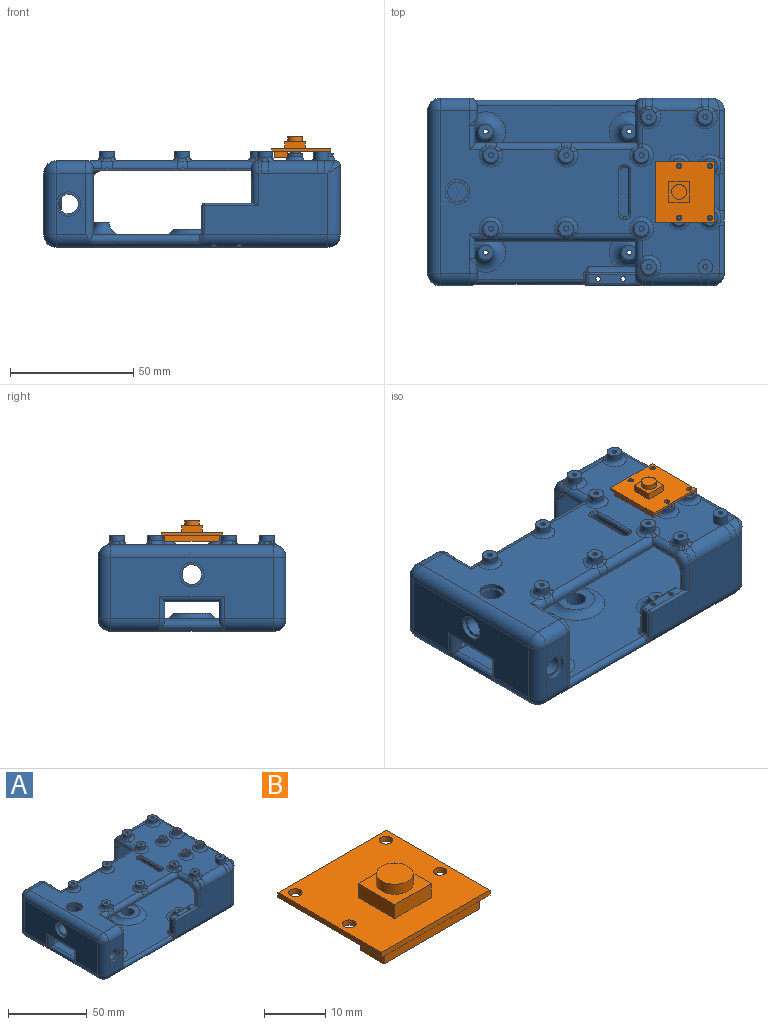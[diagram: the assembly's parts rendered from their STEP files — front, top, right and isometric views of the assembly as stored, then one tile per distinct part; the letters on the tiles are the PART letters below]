
ASSEMBLY  parts=2 mates=1
PART A: 360 faces, bbox 123.4x78.5x40.3 mm
  f0: plane 28x10mm, normal (1,0,0), area 97.8mm2, adj f1,f355,f356,f357,f358,f359
  f1: torus R=7mm, axis (-1,0,0), area 28.3mm2, adj f0,f2,f355,f359
  f2: cylinder r=5mm len=5mm, axis (-1,0,0), area 15.7mm2, adj f1,f3,f353,f354
  f3: plane 16x2mm, normal (0,-1,0), area 32mm2, adj f2,f4,f352,f359
  f4: cylinder r=2mm len=16mm, axis (0,0,1), area 50.3mm2, adj f3,f5,f351,f354
  f5: plane 26x7.1mm, normal (-1,0,0), area 125.8mm2, adj f4,f6,f348,f349,f350,f351,f353,f354
  f6: plane 112.82x71.05mm, normal (0,0,1), area 5628.9mm2, adj f5,f7,f314,f315,f316,f318,f319,f320
  f7: torus R=7mm, axis (-1,0,0), area 20.9mm2, adj f6,f8,f314,f344
  f8: cylinder r=2mm len=16mm, axis (0,0,1), area 50.3mm2, adj f7,f9,f313,f314
  f9: plane 16x2mm, normal (0,1,0), area 32mm2, adj f8,f10,f312,f344
  f10: cylinder r=2mm len=16mm, axis (0,0,-1), area 50.3mm2, adj f9,f11,f309,f310
  f11: plane 28x10mm, normal (1,0,0), area 97.8mm2, adj f10,f12,f309,f310,f355,f357
  f12: cylinder r=5mm len=28mm, axis (0,0,-1), area 208.1mm2, adj f11,f13,f307,f308
  f13: sphere r=5mm, area 39.3mm2, adj f12,f14,f357
  f14: cylinder r=5mm len=110mm, axis (1,0,0), area 689.2mm2, adj f13,f15,f288,f289,f304,f305,f306,f307
  f15: cylinder r=1mm len=17.66mm, axis (0,0,1), area 108.2mm2, adj f14,f16
  f16: plane 20.27x3.4mm, normal (0,0,1), area 59.2mm2, adj f15,f17,f274,f275,f276,f285,f286,f287
  f17: plane 30x16mm, normal (0,1,0), area 469.6mm2, adj f16,f18,f274,f287,f314,f316
  f18: cylinder r=5mm len=29mm, axis (1,0,0), area 227.4mm2, adj f17,f19,f20,f314,f353
  f19: bspline ~4.02x2.53mm, area 6.1mm2, adj f18,f20,f274,f275
  f20: torus R=6mm, axis (1,0,0), area 8.3mm2, adj f18,f19,f21,f273
  f21: cylinder r=1mm len=10mm, axis (0,-1,0), area 15.7mm2, adj f20,f22,f272,f273,f353
  f22: cylinder r=3mm len=9.84mm, axis (0,1,0), area 42.6mm2, adj f21,f23,f46,f47,f214,f215
  f23: bspline ~4.03x2.8mm, area 5.5mm2, adj f22,f24,f41,f45
  f24: bspline ~3.52x1.71mm, area 5.2mm2, adj f23,f25,f41,f46
  f25: bspline ~2.95x2.06mm, area 1.9mm2, adj f24,f26,f40,f41
  f26: cylinder r=3mm len=2.85mm, axis (0,1,0), area 3.6mm2, adj f25,f27,f46,f273
  f27: torus R=2mm, axis (1,0,0), area 28.4mm2, adj f26,f28,f40,f273,f275
  f28: cylinder r=5mm len=4.88mm, axis (1,0,0), area 7mm2, adj f27,f29,f39,f307
  f29: bspline ~3.05x2.15mm, area 2.1mm2, adj f28,f30,f40,f41
  f30: bspline ~3.36x1.78mm, area 5.2mm2, adj f29,f31,f39,f41
  f31: bspline ~4.17x3.08mm, area 6mm2, adj f30,f32,f41,f45
  f32: cylinder r=5mm len=19.94mm, axis (1,0,0), area 154.7mm2, adj f31,f33,f39,f215,f307
  f33: bspline ~5.28x5.26mm, area 22.2mm2, adj f32,f34,f38,f307
  f34: cylinder r=3mm len=6mm, axis (0,0,-1), area 75.4mm2, adj f33,f35,f215
  f35: plane 6x6mm, normal (0,0,1), area 25.1mm2, adj f34,f36
  f36: cylinder r=1mm len=4mm, axis (0,0,-1), area 25.1mm2, adj f35,f37
  f37: plane 2x2mm, normal (0,0,1), area 3.1mm2, adj f36
  f38: cylinder r=5mm len=5mm, axis (1,0,0), area 24.1mm2, adj f33,f215,f307,f308
  f39: bspline ~5.28x5.26mm, area 18.1mm2, adj f28,f30,f32,f307
  f40: bspline ~2.93x2.68mm, area 3.1mm2, adj f25,f27,f29,f41
  f41: cylinder r=3mm len=6mm, axis (0,0,-1), area 44.3mm2, adj f23,f24,f25,f29,f30,f31,f40,f42
  f42: plane 6x6mm, normal (0,0,1), area 25.1mm2, adj f41,f43
  f43: cylinder r=1mm len=4mm, axis (0,0,-1), area 25.1mm2, adj f42,f44
  f44: plane 2x2mm, normal (0,0,1), area 3.1mm2, adj f43
  f45: torus R=4.8mm, axis (0,0,1), area 27.9mm2, adj f23,f31,f41,f215
  f46: bspline ~4.49x3.34mm, area 10.4mm2, adj f22,f24,f26,f273
  f47: cylinder r=3mm len=27.11mm, axis (1,0,0), area 120.5mm2, adj f22,f48,f207,f208,f214,f215,f272
  f48: bspline ~4.91x3.2mm, area 12.2mm2, adj f47,f49,f206,f272
  f49: cylinder r=3mm len=26.23mm, axis (1,0,0), area 120.5mm2, adj f48,f50,f199,f200,f215,f272
  f50: bspline ~4.91x3.2mm, area 12.2mm2, adj f49,f51,f198,f272
  f51: cylinder r=3mm len=6.46mm, axis (1,0,0), area 24.8mm2, adj f50,f52,f192,f215,f272
  f52: cylinder r=2mm len=10mm, axis (0,-1,0), area 50.3mm2, adj f51,f53,f215,f272,f353
  f53: bspline ~4.71x4.31mm, area 19.5mm2, adj f52,f54,f190,f191
  f54: cylinder r=3mm len=6mm, axis (0,-1,0), area 19.8mm2, adj f53,f55,f215,f323
  f55: torus R=2mm, axis (-1,0,0), area 28.9mm2, adj f54,f56,f322,f323
  f56: cylinder r=5mm len=12mm, axis (1,0,0), area 94.2mm2, adj f55,f57,f215,f305
  f57: sphere r=5mm, area 39.3mm2, adj f56,f58,f189
  f58: cylinder r=5mm len=25mm, axis (0,0,1), area 196.3mm2, adj f57,f59,f304,f305
  f59: plane 66x25mm, normal (-1,0,0), area 1337.5mm2, adj f58,f60,f180,f181,f186,f187,f188,f189
  f60: cylinder r=5mm len=10mm, axis (1,0,0), area 56.5mm2, adj f59,f61
  f61: plane 10x10mm, normal (-1,0,0), area 28.3mm2, adj f60,f62
  f62: cylinder r=4mm len=8mm, axis (1,0,0), area 138.2mm2, adj f61,f63
  f63: plane 16.26x13.46mm, normal (1,0,0), area 103.7mm2, adj f62,f64,f171,f172,f177,f178,f179
  f64: plane 15x12.2mm, normal (0,0,-1), area 103.7mm2, adj f63,f65,f68
  f65: cylinder r=4mm len=8mm, axis (0,0,-1), area 138.2mm2, adj f64,f66
  f66: plane 10x10mm, normal (0,0,1), area 28.3mm2, adj f65,f67
  f67: cylinder r=5mm len=10mm, axis (0,0,-1), area 56.5mm2, adj f66,f215
  f68: torus R=12.2mm, axis (0,0,1), area 222.9mm2, adj f64,f69,f70,f159,f170,f171,f179,f353
  f69: sphere r=5mm, area 20.7mm2, adj f68,f70,f171,f172
  f70: cylinder r=5mm len=21.5mm, axis (0,-1,0), area 153.7mm2, adj f68,f69,f71,f158,f332,f353
  f71: torus R=10.86mm, axis (0,1,0), area 104.7mm2, adj f70,f72,f154,f155,f158,f332,f333
  f72: bspline ~15.69x2.44mm, area 38.6mm2, adj f71,f73,f334,f335
  f73: cylinder r=2mm len=2mm, axis (0,0,-1), area 3.6mm2, adj f72,f74,f154,f335
  f74: torus R=7mm, axis (-1,0,0), area 18.5mm2, adj f73,f75,f158,f335
  f75: bspline ~4.71x4.31mm, area 19.5mm2, adj f74,f76,f153,f158
  f76: cylinder r=2mm len=10mm, axis (0,-1,0), area 50.3mm2, adj f75,f77,f152,f215,f353
  f77: cylinder r=3mm len=6.46mm, axis (-1,0,0), area 24.8mm2, adj f76,f78,f151,f152,f215
  f78: bspline ~4.91x3.2mm, area 12.2mm2, adj f77,f79,f150,f152
  f79: cylinder r=3mm len=26.23mm, axis (-1,0,0), area 120.5mm2, adj f78,f80,f143,f144,f152,f215
  f80: bspline ~4.91x3.2mm, area 12.2mm2, adj f79,f81,f142,f152
  f81: cylinder r=3mm len=27.11mm, axis (-1,0,0), area 120.5mm2, adj f80,f82,f88,f135,f141,f152,f215
  f82: bspline ~3.84x2.84mm, area 5.2mm2, adj f81,f83,f84,f142
  f83: torus R=4.8mm, axis (0,0,1), area 41.9mm2, adj f82,f84,f143,f215
  f84: cylinder r=3mm len=6mm, axis (0,0,-1), area 43.9mm2, adj f82,f83,f85,f142,f143
  f85: plane 6x6mm, normal (0,0,1), area 25.1mm2, adj f84,f86
  f86: cylinder r=1mm len=4mm, axis (0,0,-1), area 25.1mm2, adj f85,f87
  f87: plane 2x2mm, normal (0,0,1), area 3.1mm2, adj f86
  f88: cylinder r=3mm len=9.84mm, axis (0,1,0), area 42.6mm2, adj f81,f89,f133,f134,f135,f215
  f89: cylinder r=1mm len=10mm, axis (0,-1,0), area 15.7mm2, adj f88,f90,f129,f152,f353
  f90: plane 6.25x2.72mm, normal (-1,0,0), area 3.2mm2, adj f89,f91,f128,f129,f133,f338
  f91: torus R=2mm, axis (1,0,0), area 28.4mm2, adj f90,f92,f127,f128,f338
  f92: cylinder r=5mm len=4.88mm, axis (1,0,0), area 7mm2, adj f91,f93,f125,f126
  f93: plane 28x25.01mm, normal (0,1,0), area 700mm2, adj f92,f94,f104,f105,f115,f125,f338,f356
  f94: cylinder r=5mm len=5mm, axis (1,0,0), area 22.2mm2, adj f93,f95,f103,f104,f215
  f95: bspline ~4.17x3.08mm, area 6mm2, adj f94,f96,f98,f99
  f96: torus R=4.8mm, axis (0,0,1), area 44.4mm2, adj f95,f97,f99,f215
  f97: bspline ~4.17x3.08mm, area 6mm2, adj f96,f98,f99,f105
  f98: bspline ~3.36x1.78mm, area 5.2mm2, adj f95,f97,f99,f104
  f99: cylinder r=3mm len=6mm, axis (0,0,-1), area 42.6mm2, adj f95,f96,f97,f98,f100
  f100: plane 6x6mm, normal (0,0,1), area 25.1mm2, adj f99,f101
  f101: cylinder r=1mm len=4mm, axis (0,0,-1), area 25.1mm2, adj f100,f102
  f102: plane 2x2mm, normal (0,0,1), area 3.1mm2, adj f101
  f103: bspline ~5.23x5mm, area 10.8mm2, adj f94,f355,f356
  f104: bspline ~5.28x5.26mm, area 18.1mm2, adj f93,f94,f98,f105
  f105: cylinder r=5mm len=19.94mm, axis (1,0,0), area 152.9mm2, adj f93,f97,f104,f106,f125,f215
  f106: bspline ~4.17x3.08mm, area 6mm2, adj f105,f107,f108,f109
  f107: torus R=4.8mm, axis (0,0,1), area 27.9mm2, adj f106,f109,f134,f215
  f108: bspline ~3.36x1.78mm, area 5.2mm2, adj f106,f109,f125,f126
  f109: cylinder r=3mm len=6mm, axis (0,0,-1), area 44.3mm2, adj f106,f107,f108,f110,f111,f114,f126,f127
  f110: bspline ~3.26x1.69mm, area 5.2mm2, adj f109,f114,f133,f134
  f111: plane 6x6mm, normal (0,0,1), area 25.1mm2, adj f109,f112
  f112: cylinder r=1mm len=4mm, axis (0,0,-1), area 25.1mm2, adj f111,f113
  f113: plane 2x2mm, normal (0,0,1), area 3.1mm2, adj f112
  f114: bspline ~2.95x2.06mm, area 1.9mm2, adj f109,f110,f127,f128
  f115: cylinder r=5mm len=110mm, axis (1,0,0), area 617.5mm2, adj f93,f116,f123,f124,f289,f336,f337,f338
  f116: plane 25x12mm, normal (0,1,0), area 221.5mm2, adj f115,f117,f120,f180,f336
  f117: cylinder r=5mm len=10mm, axis (0,-1,0), area 56.5mm2, adj f116,f118
  f118: plane 10x10mm, normal (0,1,0), area 28.3mm2, adj f117,f119
  f119: cylinder r=4mm len=8mm, axis (0,-1,0), area 138.2mm2, adj f118,f155
  f120: cylinder r=5mm len=12mm, axis (1,0,0), area 94.2mm2, adj f116,f121,f122,f215
  f121: sphere r=5mm, area 53.5mm2, adj f120,f180,f189
  f122: torus R=2mm, axis (-1,0,0), area 28.9mm2, adj f120,f153,f335,f336
  f123: sphere r=5mm, area 53.5mm2, adj f115,f180,f188
  f124: sphere r=5mm, area 25mm2, adj f115,f356,f357
  f125: bspline ~5.28x5.26mm, area 18.1mm2, adj f92,f93,f105,f108
  f126: bspline ~3.05x2.15mm, area 2.1mm2, adj f92,f108,f109,f127
  f127: bspline ~2.93x2.68mm, area 3.1mm2, adj f91,f109,f114,f126
  f128: cylinder r=3mm len=2.85mm, axis (0,1,0), area 3.6mm2, adj f90,f91,f114,f133
  f129: torus R=6mm, axis (1,0,0), area 8.3mm2, adj f89,f90,f130,f350
  f130: bspline ~4.02x2.53mm, area 6.1mm2, adj f129,f131,f338,f350
  f131: cylinder r=1mm len=16mm, axis (0,0,1), area 33.5mm2, adj f130,f132,f338,f349
  f132: bspline ~4.02x2.53mm, area 6.1mm2, adj f131,f338,f340,f348
  f133: bspline ~4.49x3.34mm, area 10.4mm2, adj f88,f90,f110,f128
  f134: bspline ~4.03x2.8mm, area 5.5mm2, adj f88,f107,f109,f110
  f135: bspline ~2.91x2.77mm, area 4.5mm2, adj f81,f88,f136,f140,f141
  f136: cylinder r=3mm len=6mm, axis (0,0,-1), area 42.5mm2, adj f135,f137,f140,f141
  f137: plane 6x6mm, normal (0,0,1), area 25.1mm2, adj f136,f138
  f138: cylinder r=1mm len=4mm, axis (0,0,-1), area 25.1mm2, adj f137,f139
  f139: plane 2x2mm, normal (0,0,1), area 3.1mm2, adj f138
  f140: torus R=4.8mm, axis (0,0,1), area 52.4mm2, adj f135,f136,f141,f215
  f141: bspline ~4.14x2.91mm, area 6.2mm2, adj f81,f135,f136,f140
  f142: bspline ~4.25x1.65mm, area 6.3mm2, adj f80,f82,f84,f143
  f143: bspline ~3.84x2.84mm, area 5.2mm2, adj f79,f83,f84,f142
  f144: bspline ~3.84x2.84mm, area 5.2mm2, adj f79,f145,f146,f150
  f145: torus R=4.8mm, axis (0,0,1), area 41.9mm2, adj f144,f146,f151,f215
  f146: cylinder r=3mm len=6mm, axis (0,0,-1), area 43.9mm2, adj f144,f145,f147,f150,f151
  f147: plane 6x6mm, normal (0,0,1), area 25.1mm2, adj f146,f148
  f148: cylinder r=1mm len=4mm, axis (0,0,-1), area 25.1mm2, adj f147,f149
  f149: plane 2x2mm, normal (0,0,1), area 3.1mm2, adj f148
  f150: bspline ~4.25x1.65mm, area 6.3mm2, adj f78,f144,f146,f151
  f151: bspline ~3.84x2.84mm, area 5.2mm2, adj f77,f145,f146,f150
  f152: plane 68x1.13mm, normal (0,1,0), area 66.6mm2, adj f76,f77,f78,f79,f80,f81,f89,f353
  f153: cylinder r=3mm len=6mm, axis (0,-1,0), area 19.8mm2, adj f75,f122,f215,f335
  f154: plane 1.24x1.15mm, normal (0,-1,0), area 0.7mm2, adj f71,f73,f158
  f155: plane 15x15mm, normal (0,-1,0), area 126.4mm2, adj f71,f119,f156
  f156: cylinder r=7.5mm len=17.7mm, axis (0,1,0), area 267.7mm2, adj f155,f157,f332
  f157: plane 12.69x3.5mm, normal (0,1,0), area 31.3mm2, adj f156,f332
  f158: cylinder r=5mm len=11.94mm, axis (-1,0,0), area 69.1mm2, adj f70,f71,f74,f75,f154,f353
  f159: cylinder r=5mm len=21.5mm, axis (0,-1,0), area 153.7mm2, adj f68,f160,f170,f190,f326,f353
  f160: torus R=10.86mm, axis (0,-1,0), area 104.7mm2, adj f159,f161,f163,f164,f190,f325,f326
  f161: plane 1.24x1.15mm, normal (0,1,0), area 0.7mm2, adj f160,f162,f190
  f162: cylinder r=2mm len=2mm, axis (0,0,1), area 3.6mm2, adj f161,f163,f191,f323
  f163: bspline ~15.46x2.44mm, area 38.6mm2, adj f160,f162,f323,f324
  f164: plane 15x15mm, normal (0,1,0), area 126.4mm2, adj f160,f165,f167
  f165: cylinder r=7.5mm len=17.7mm, axis (0,-1,0), area 267.7mm2, adj f164,f166,f326
  f166: plane 12.69x3.5mm, normal (0,-1,0), area 31.3mm2, adj f165,f326
  f167: cylinder r=4mm len=8mm, axis (0,1,0), area 138.2mm2, adj f164,f168
  f168: plane 10x10mm, normal (0,-1,0), area 28.3mm2, adj f167,f169
  f169: cylinder r=5mm len=10mm, axis (0,1,0), area 56.5mm2, adj f168,f305
  f170: sphere r=5mm, area 20.7mm2, adj f68,f159,f178,f179
  f171: bspline ~5.35x3.56mm, area 2.6mm2, adj f63,f68,f69
  f172: torus R=10.86mm, axis (-1,0,0), area 40.4mm2, adj f63,f69,f173,f332
  f173: cylinder r=7.5mm len=11.69mm, axis (0,0,1), area 43.2mm2, adj f172,f174,f175,f176,f177,f178,f326,f332
  f174: plane 22x3mm, normal (0,0,-1), area 64.2mm2, adj f173,f175,f176,f186,f328,f330
  f175: cylinder r=1mm len=9.31mm, axis (0,1,0), area 12.4mm2, adj f173,f174,f331,f332
  f176: cylinder r=1mm len=9.31mm, axis (0,1,0), area 12.4mm2, adj f173,f174,f326,f327
  f177: cylinder r=7.5mm len=11.69mm, axis (1,0,0), area 0mm2, adj f63,f173
  f178: torus R=10.86mm, axis (-1,0,0), area 40.4mm2, adj f63,f170,f173,f326
  f179: bspline ~5.35x3.56mm, area 2.6mm2, adj f63,f68,f170
  f180: cylinder r=5mm len=25mm, axis (0,0,1), area 196.3mm2, adj f59,f116,f121,f123
  f181: cylinder r=2mm len=9mm, axis (0,0,-1), area 25.1mm2, adj f59,f182,f186,f328
  f182: torus R=3mm, axis (0,-1,0), area 9mm2, adj f181,f183,f188,f328
  f183: cylinder r=2mm len=26mm, axis (0,-1,0), area 120.1mm2, adj f182,f184,f185,f188,f328,f330
  f184: torus R=3mm, axis (0,-1,0), area 9mm2, adj f183,f187,f188,f330
  f185: plane 22x21.66mm, normal (0,0,1), area 476.5mm2, adj f183,f328,f329,f330
  f186: cylinder r=2mm len=26mm, axis (0,-1,0), area 75.4mm2, adj f59,f174,f181,f187
  f187: cylinder r=2mm len=9mm, axis (0,0,1), area 25.1mm2, adj f59,f184,f186,f330
  f188: cylinder r=5mm len=66mm, axis (0,-1,0), area 390.3mm2, adj f59,f123,f182,f183,f184,f289,f304
  f189: cylinder r=5mm len=66mm, axis (0,-1,0), area 518.4mm2, adj f57,f59,f121,f215
  f190: cylinder r=5mm len=11.94mm, axis (1,0,0), area 69.1mm2, adj f53,f159,f160,f161,f191,f353
  f191: torus R=7mm, axis (-1,0,0), area 18.5mm2, adj f53,f162,f190,f323
  f192: bspline ~3.84x2.84mm, area 5.2mm2, adj f51,f193,f194,f198
  f193: torus R=4.8mm, axis (0,0,1), area 41.9mm2, adj f192,f194,f199,f215
  f194: cylinder r=3mm len=6mm, axis (0,0,-1), area 43.9mm2, adj f192,f193,f195,f198,f199
  f195: plane 6x6mm, normal (0,0,1), area 25.1mm2, adj f194,f196
  f196: cylinder r=1mm len=4mm, axis (0,0,-1), area 25.1mm2, adj f195,f197
  f197: plane 2x2mm, normal (0,0,1), area 3.1mm2, adj f196
  f198: bspline ~4.4x1.66mm, area 6.3mm2, adj f50,f192,f194,f199
  f199: bspline ~3.84x2.84mm, area 5.2mm2, adj f49,f193,f194,f198
  f200: bspline ~3.84x2.84mm, area 5.2mm2, adj f49,f201,f202,f206
  f201: torus R=4.8mm, axis (0,0,1), area 41.9mm2, adj f200,f202,f207,f215
  f202: cylinder r=3mm len=6mm, axis (0,0,-1), area 43.9mm2, adj f200,f201,f203,f206,f207
  f203: plane 6x6mm, normal (0,0,1), area 25.1mm2, adj f202,f204
  f204: cylinder r=1mm len=4mm, axis (0,0,-1), area 25.1mm2, adj f203,f205
  f205: plane 2x2mm, normal (0,0,1), area 3.1mm2, adj f204
  f206: bspline ~4.4x1.66mm, area 6.3mm2, adj f48,f200,f202,f207
  f207: bspline ~3.84x2.84mm, area 5.2mm2, adj f47,f201,f202,f206
  f208: bspline ~4.14x2.91mm, area 6.2mm2, adj f47,f209,f210,f214
  f209: torus R=4.8mm, axis (0,0,1), area 52.4mm2, adj f208,f210,f214,f215
  f210: cylinder r=3mm len=6mm, axis (0,0,-1), area 42.5mm2, adj f208,f209,f211,f214
  f211: plane 6x6mm, normal (0,0,1), area 25.1mm2, adj f210,f212
  f212: cylinder r=1mm len=4mm, axis (0,0,-1), area 25.1mm2, adj f211,f213
  f213: plane 2x2mm, normal (0,0,1), area 3.1mm2, adj f212
  f214: bspline ~2.91x2.77mm, area 4.5mm2, adj f22,f47,f208,f209,f210
  f215: plane 113x66mm, normal (0,0,1), area 4218.9mm2, adj f22,f32,f34,f38,f45,f47,f49,f51
  f216: torus R=4.8mm, axis (0,0,1), area 63.3mm2, adj f215,f217,f223
  f217: cylinder r=3mm len=6mm, axis (0,0,-1), area 22.6mm2, adj f216,f218
  f218: plane 6x6mm, normal (0,0,1), area 15.7mm2, adj f217,f219
  f219: cylinder r=2mm len=4mm, axis (0,0,1), area 12.6mm2, adj f218,f220
  f220: plane 4x4mm, normal (0,0,1), area 11.4mm2, adj f219,f221
  f221: cylinder r=0.6mm len=4mm, axis (0,0,1), area 15.1mm2, adj f220,f222
  f222: plane 1.2x1.2mm, normal (0,0,1), area 1.1mm2, adj f221
  f223: bspline ~8.68x2.41mm, area 16.7mm2, adj f216,f224,f355
  f224: plane 6x0.15mm, normal (1,0,0), area 0.5mm2, adj f223,f355
  f225: torus R=4.8mm, axis (0,0,1), area 63.3mm2, adj f215,f226,f228
  f226: bspline ~8.68x2.41mm, area 16.7mm2, adj f225,f227,f355
  f227: plane 6x0.15mm, normal (1,0,0), area 0.5mm2, adj f226,f355
  f228: cylinder r=3mm len=6mm, axis (0,0,-1), area 22.6mm2, adj f225,f229
  f229: plane 6x6mm, normal (0,0,1), area 15.7mm2, adj f228,f230
  f230: cylinder r=2mm len=4mm, axis (0,0,1), area 12.6mm2, adj f229,f231
  f231: plane 4x4mm, normal (0,0,1), area 11.4mm2, adj f230,f232
  f232: cylinder r=0.6mm len=4mm, axis (0,0,1), area 15.1mm2, adj f231,f233
  f233: plane 1.2x1.2mm, normal (0,0,1), area 1.1mm2, adj f232
  f234: torus R=4.8mm, axis (0,0,1), area 64.9mm2, adj f215,f235
  f235: cylinder r=3mm len=6mm, axis (0,0,-1), area 22.6mm2, adj f234,f236
  f236: plane 6x6mm, normal (0,0,1), area 15.7mm2, adj f235,f237
  f237: cylinder r=2mm len=4mm, axis (0,0,1), area 12.6mm2, adj f236,f238
  f238: plane 4x4mm, normal (0,0,1), area 11.4mm2, adj f237,f239
  f239: cylinder r=0.6mm len=4mm, axis (0,0,1), area 15.1mm2, adj f238,f240
  f240: plane 1.2x1.2mm, normal (0,0,1), area 1.1mm2, adj f239
  f241: torus R=4.8mm, axis (0,0,1), area 64.9mm2, adj f215,f242
  f242: cylinder r=3mm len=6mm, axis (0,0,-1), area 22.6mm2, adj f241,f243
  f243: plane 6x6mm, normal (0,0,1), area 15.7mm2, adj f242,f244
  f244: cylinder r=2mm len=4mm, axis (0,0,1), area 12.6mm2, adj f243,f245
  f245: plane 4x4mm, normal (0,0,1), area 11.4mm2, adj f244,f246
  f246: cylinder r=0.6mm len=4mm, axis (0,0,1), area 15.1mm2, adj f245,f247
  f247: plane 1.2x1.2mm, normal (0,0,1), area 1.1mm2, adj f246
  f248: cylinder r=1mm len=18mm, axis (0,1,0), area 28.3mm2, adj f215,f249,f265,f271
  f249: plane 18x2mm, normal (1,0,0), area 36mm2, adj f248,f250,f263,f264
  f250: cylinder r=1mm len=2mm, axis (0,0,1), area 3.1mm2, adj f249,f251,f262,f271
  f251: torus R=2mm, axis (0,0,1), area 3.4mm2, adj f250,f252,f263,f353
  f252: cylinder r=1mm len=1mm, axis (1,0,0), area 1.6mm2, adj f251,f253,f262,f353
  f253: torus R=2mm, axis (0,0,1), area 3.4mm2, adj f252,f254,f261,f353
  f254: cylinder r=1mm len=2mm, axis (0,0,-1), area 3.1mm2, adj f253,f255,f262,f269
  f255: plane 18x2mm, normal (-1,0,0), area 36mm2, adj f254,f256,f261,f268
  f256: cylinder r=1mm len=2mm, axis (0,0,1), area 3.1mm2, adj f255,f257,f260,f267
  f257: torus R=2mm, axis (0,0,1), area 3.4mm2, adj f256,f258,f261,f353
  f258: cylinder r=1mm len=1mm, axis (-1,0,0), area 1.6mm2, adj f257,f259,f260,f353
  f259: torus R=2mm, axis (0,0,1), area 3.4mm2, adj f258,f263,f264,f353
  f260: plane 2x1mm, normal (0,1,0), area 2mm2, adj f256,f258,f264,f266
  f261: cylinder r=1mm len=18mm, axis (0,-1,0), area 28.3mm2, adj f253,f255,f257,f353
  f262: plane 2x1mm, normal (0,-1,0), area 2mm2, adj f250,f252,f254,f270
  f263: cylinder r=1mm len=18mm, axis (0,1,0), area 28.3mm2, adj f249,f251,f259,f353
  f264: cylinder r=1mm len=2mm, axis (0,0,-1), area 3.1mm2, adj f249,f259,f260,f265
  f265: torus R=2mm, axis (0,0,1), area 3.4mm2, adj f215,f248,f264,f266
  f266: cylinder r=1mm len=1mm, axis (-1,0,0), area 1.6mm2, adj f215,f260,f265,f267
  f267: torus R=2mm, axis (0,0,1), area 3.4mm2, adj f215,f256,f266,f268
  f268: cylinder r=1mm len=18mm, axis (0,-1,0), area 28.3mm2, adj f215,f255,f267,f269
  f269: torus R=2mm, axis (0,0,1), area 3.4mm2, adj f215,f254,f268,f270
  f270: cylinder r=1mm len=1mm, axis (1,0,0), area 1.6mm2, adj f215,f262,f269,f271
  f271: torus R=2mm, axis (0,0,1), area 3.4mm2, adj f215,f248,f250,f270
  f272: plane 68x1.13mm, normal (0,-1,0), area 66.6mm2, adj f21,f47,f48,f49,f50,f51,f52,f353
  f273: plane 6.25x2.72mm, normal (-1,0,0), area 3.2mm2, adj f20,f21,f26,f27,f46,f275
  f274: cylinder r=1mm len=8.2mm, axis (0,0,1), area 17.2mm2, adj f16,f17,f19,f275
  f275: cylinder r=3mm len=13.2mm, axis (0,0,1), area 42.4mm2, adj f16,f19,f27,f273,f274,f276,f307
  f276: cylinder r=1mm len=22mm, axis (1,0,0), area 32.8mm2, adj f16,f275,f277,f307
  f277: sphere r=1mm, area 1.6mm2, adj f276,f278,f285
  f278: cylinder r=1mm len=11.37mm, axis (0,0,-1), area 17.9mm2, adj f277,f279,f281,f307
  f279: bspline ~1.05x1.03mm, area 0.5mm2, adj f278,f280,f306,f307
  f280: torus R=3mm, axis (-1,0,0), area 4.6mm2, adj f279,f281,f306,f320,f321
  f281: plane 11.37x3.4mm, normal (-1,0,0), area 37mm2, adj f278,f280,f282,f285,f320
  f282: cylinder r=1mm len=10.8mm, axis (0,0,1), area 17mm2, adj f281,f283,f284,f319
  f283: plane 19x11.07mm, normal (0,1,0), area 210.3mm2, adj f282,f286,f287,f316,f319
  f284: sphere r=1mm, area 2.1mm2, adj f282,f285,f286
  f285: cylinder r=1mm len=3.4mm, axis (0,1,0), area 5.3mm2, adj f16,f277,f281,f284
  f286: cylinder r=1mm len=19mm, axis (1,0,0), area 29.8mm2, adj f16,f283,f284,f287
  f287: plane 12.07x2.4mm, normal (1,0,0), area 25.8mm2, adj f16,f17,f283,f286,f316
  f288: cylinder r=1mm len=17.66mm, axis (0,0,1), area 108.2mm2, adj f14,f16
  f289: plane 110x66mm, normal (0,0,-1), area 7168.9mm2, adj f14,f115,f188,f290,f294,f296,f298,f300
  f290: cylinder r=1mm len=10mm, axis (0,0,-1), area 62.8mm2, adj f289,f291
  f291: plane 6x6mm, normal (0,0,1), area 25.1mm2, adj f290,f292,f315
  f292: cylinder r=3mm len=4.36mm, axis (0,0,-1), area 0mm2, adj f291,f293
  f293: bspline ~12.57x5.47mm, area 41.3mm2, adj f292,f315,f316
  f294: cylinder r=1mm len=10mm, axis (0,0,-1), area 62.8mm2, adj f289,f295
  f295: plane 6x6mm, normal (0,0,1), area 25.1mm2, adj f294,f346
  f296: cylinder r=1mm len=10mm, axis (0,0,-1), area 62.8mm2, adj f289,f297
  f297: plane 6x6mm, normal (0,0,1), area 25.1mm2, adj f296,f345
  f298: cylinder r=1mm len=10mm, axis (0,0,-1), area 62.8mm2, adj f289,f299
  f299: plane 6x6mm, normal (0,0,1), area 25.1mm2, adj f298,f341
  f300: cylinder r=5mm len=10mm, axis (0,0,1), area 56.5mm2, adj f289,f301
  f301: plane 10x10mm, normal (0,0,-1), area 28.3mm2, adj f300,f302
  f302: cylinder r=4mm len=8mm, axis (0,0,1), area 138.2mm2, adj f301,f303
  f303: plane 15x15mm, normal (0,0,1), area 126.4mm2, adj f302,f347
  f304: sphere r=5mm, area 39.3mm2, adj f14,f58,f188
  f305: plane 25x12mm, normal (0,-1,0), area 221.5mm2, adj f14,f56,f58,f169,f322
  f306: bspline ~3.46x1.97mm, area 2.1mm2, adj f14,f279,f280
  f307: plane 50.03x25.02mm, normal (0,-1,0), area 959.6mm2, adj f12,f14,f28,f32,f33,f38,f39,f275
  f308: bspline ~5.91x5mm, area 10.8mm2, adj f12,f38,f355
  f309: torus R=7mm, axis (-1,0,0), area 28.3mm2, adj f10,f11,f312,f355
  f310: torus R=7mm, axis (-1,0,0), area 14.3mm2, adj f10,f11,f311,f344
  f311: bspline ~5.58x5.15mm, area 19mm2, adj f310,f342,f344,f357
  f312: cylinder r=5mm len=5mm, axis (1,0,0), area 15.7mm2, adj f9,f309,f313,f353
  f313: torus R=7mm, axis (-1,0,0), area 20.9mm2, adj f8,f312,f314,f353
  f314: plane 26x7.1mm, normal (-1,0,0), area 125.8mm2, adj f6,f7,f8,f17,f18,f313,f316,f353
  f315: torus R=8mm, axis (0,0,1), area 176.2mm2, adj f6,f291,f293
  f316: cylinder r=5mm len=49mm, axis (-1,0,0), area 287.6mm2, adj f6,f17,f283,f287,f293,f314,f317,f319
  f317: torus R=6mm, axis (-1,0,0), area 1.1mm2, adj f316,f318,f319
  f318: bspline ~3.27x1.73mm, area 0.7mm2, adj f6,f317,f319
  f319: torus R=2mm, axis (0,0,1), area 2.3mm2, adj f6,f282,f283,f316,f317,f318,f320
  f320: cylinder r=1mm len=1.64mm, axis (0,-1,0), area 2.6mm2, adj f6,f280,f281,f319
  f321: cylinder r=2mm len=43.55mm, axis (1,0,0), area 199.1mm2, adj f6,f14,f280,f322
  f322: cylinder r=3mm len=28.33mm, axis (0,0,1), area 121.7mm2, adj f6,f14,f55,f305,f321,f323
  f323: plane 27x4.39mm, normal (1,0,0), area 36.6mm2, adj f6,f54,f55,f162,f163,f191,f322,f324
  f324: cylinder r=2mm len=5.15mm, axis (0,0,-1), area 16.2mm2, adj f6,f163,f323,f325
  f325: plane 12x5.15mm, normal (0,1,0), area 29.3mm2, adj f6,f160,f324,f326
  f326: plane 27.72x21.22mm, normal (1,0,0), area 209.5mm2, adj f6,f159,f160,f165,f166,f173,f176,f178
  f327: cylinder r=1mm len=8mm, axis (0,0,1), area 11.8mm2, adj f6,f176,f326,f328
  f328: plane 23x7.9mm, normal (0,1,0), area 32.7mm2, adj f6,f174,f181,f182,f183,f185,f327,f329
  f329: plane 22x0.5mm, normal (-1,0,0), area 11mm2, adj f6,f185,f328,f330
  f330: plane 23x7.9mm, normal (0,-1,0), area 32.7mm2, adj f6,f174,f183,f184,f185,f187,f329,f331
  f331: cylinder r=1mm len=8mm, axis (0,0,-1), area 11.8mm2, adj f6,f175,f330,f332
  f332: plane 27.72x21.22mm, normal (1,0,0), area 209.5mm2, adj f6,f70,f71,f156,f157,f172,f173,f175
  f333: plane 12x5.15mm, normal (0,-1,0), area 29.3mm2, adj f6,f71,f332,f334
  f334: cylinder r=2mm len=5.15mm, axis (0,0,-1), area 16.2mm2, adj f6,f72,f333,f335
  f335: plane 27x4.39mm, normal (1,0,0), area 36.6mm2, adj f6,f72,f73,f74,f122,f153,f334,f336
  f336: cylinder r=3mm len=28.33mm, axis (0,0,1), area 121.7mm2, adj f6,f115,f116,f122,f335,f337
  f337: cylinder r=2mm len=65.09mm, axis (1,0,0), area 297mm2, adj f6,f115,f336,f338
  f338: cylinder r=3mm len=28.33mm, axis (0,0,1), area 89.6mm2, adj f6,f90,f91,f93,f115,f130,f131,f132
  f339: plane 1.68x1.68mm, normal (-1,0,0), area 1.2mm2, adj f6,f338,f340
  f340: torus R=6mm, axis (1,0,0), area 5.2mm2, adj f6,f132,f339,f341,f348
  f341: torus R=8mm, axis (0,0,1), area 236.1mm2, adj f6,f299,f340,f348
  f342: cylinder r=2mm len=46mm, axis (0,1,0), area 211.6mm2, adj f6,f311,f343,f357
  f343: bspline ~5.97x5.2mm, area 19mm2, adj f342,f352,f357,f358
  f344: cylinder r=5mm len=5mm, axis (-1,0,0), area 14.2mm2, adj f6,f7,f9,f310,f311
  f345: torus R=8mm, axis (0,0,1), area 237.7mm2, adj f6,f297
  f346: torus R=8mm, axis (0,0,1), area 237.7mm2, adj f6,f295
  f347: torus R=11.71mm, axis (0,0,1), area 295.7mm2, adj f6,f303
  f348: cylinder r=5mm len=29mm, axis (1,0,0), area 226.4mm2, adj f5,f6,f132,f340,f341,f349
  f349: plane 28.73x16mm, normal (0,-1,0), area 459.7mm2, adj f5,f131,f348,f350
  f350: cylinder r=5mm len=29mm, axis (-1,0,0), area 227.4mm2, adj f5,f129,f130,f349,f353
  f351: torus R=7mm, axis (1,0,0), area 20.9mm2, adj f4,f5,f6,f352
  f352: cylinder r=5mm len=5mm, axis (1,0,0), area 14.2mm2, adj f3,f6,f343,f351,f358
  f353: plane 107.58x60.58mm, normal (0,0,-1), area 4610.4mm2, adj f2,f5,f18,f21,f52,f68,f70,f76
  f354: torus R=7mm, axis (1,0,0), area 20.9mm2, adj f2,f4,f5,f353
  f355: cylinder r=2mm len=66mm, axis (0,1,0), area 314.2mm2, adj f0,f1,f11,f103,f215,f223,f224,f226
  f356: cylinder r=5mm len=28mm, axis (0,0,-1), area 208.1mm2, adj f0,f93,f103,f124
  f357: cylinder r=5mm len=66mm, axis (0,1,0), area 332.7mm2, adj f0,f11,f13,f124,f289,f311,f342,f343
  f358: torus R=7mm, axis (-1,0,0), area 14.3mm2, adj f0,f343,f352,f359
  f359: cylinder r=2mm len=16mm, axis (0,0,1), area 50.3mm2, adj f0,f1,f3,f358
PART B: 22 faces, bbox 25x24x8.3 mm
  f0: plane 25x24mm, normal (0,0,1), area 514.2mm2, adj f1,f2,f3,f4,f5,f6,f7,f8
  f1: plane 24x1mm, normal (1,0,0), area 24mm2, adj f0,f2,f7,f9
  f2: plane 25x1mm, normal (0,1,0), area 25mm2, adj f0,f1,f3,f9
  f3: plane 24x1mm, normal (-1,0,0), area 24mm2, adj f0,f2,f7,f9
  f4: cylinder r=1.1mm len=2.2mm, axis (0,0,-1), area 6.9mm2, adj f0,f9
  f5: cylinder r=1.1mm len=2.2mm, axis (0,0,-1), area 6.9mm2, adj f0,f9
  f6: cylinder r=1.1mm len=2.2mm, axis (0,0,-1), area 6.9mm2, adj f0,f9
  f7: plane 25x1mm, normal (0,-1,0), area 25mm2, adj f0,f1,f3,f9
  f8: cylinder r=1.1mm len=2.2mm, axis (0,0,-1), area 6.9mm2, adj f0,f9
  f9: plane 25x24mm, normal (0,0,-1), area 463.8mm2, adj f1,f2,f3,f4,f5,f6,f7,f8
  f10: plane 8.4x2.8mm, normal (1,0,0), area 23.5mm2, adj f0,f11,f13,f14
  f11: plane 8.4x2.8mm, normal (0,1,0), area 23.5mm2, adj f0,f10,f12,f14
  f12: plane 8.4x2.8mm, normal (-1,0,0), area 23.5mm2, adj f0,f11,f13,f14
  f13: plane 8.4x2.8mm, normal (0,-1,0), area 23.5mm2, adj f0,f10,f12,f14
  f14: plane 8.4x8.4mm, normal (0,0,1), area 42.3mm2, adj f10,f11,f12,f13,f15
  f15: cylinder r=3mm len=6mm, axis (0,0,-1), area 37.7mm2, adj f14,f16
  f16: plane 6x6mm, normal (0,0,1), area 28.3mm2, adj f15
  f17: plane 5.5x2.5mm, normal (-1,0,0), area 13.7mm2, adj f9,f18,f20,f21
  f18: plane 22x2.5mm, normal (0,1,0), area 55mm2, adj f9,f17,f19,f21
  f19: plane 5.5x2.5mm, normal (1,0,0), area 13.7mm2, adj f9,f18,f20,f21
  f20: plane 22x2.5mm, normal (0,-1,0), area 55mm2, adj f9,f17,f19,f21
  f21: plane 22x5.5mm, normal (0,0,-1), area 121mm2, adj f17,f18,f19,f20
PLACE A t=(16.92,0,0)mm
PLACE B rot(axis=(0,0,-1),90deg) t=(58.67,0,34)mm
MATE fastened B.f8 <-> A.f225  axis (0,0,-1) through (68.67,-10.5,34)mm
